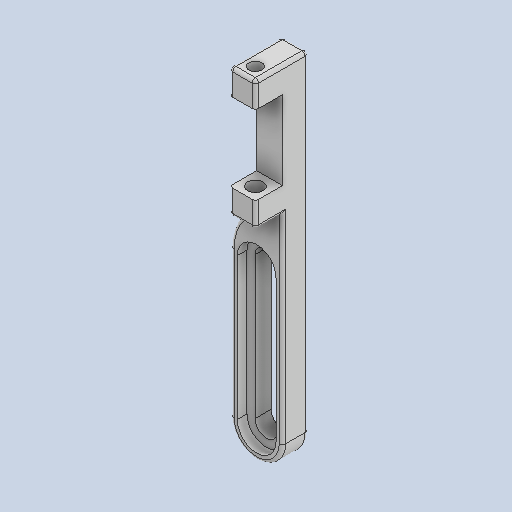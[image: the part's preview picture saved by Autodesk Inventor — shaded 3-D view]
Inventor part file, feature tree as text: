
AUTODESK INVENTOR PART (.ipt)
format: ipt  version: 2025 (Build 290162000, 162)  size: 366,592 bytes
history: native  units: mm
features: sketch x6, extrude x5, fillet x4, reference x4, other x4, plane x1
ambient origin geometry x8: Origin, YZ Plane, XZ Plane, XY Plane, X Axis, Y Axis, Z Axis, Center Point
bodies: Solid1 (feature_tree)
feature tree (24):
  plane  "Work Plane1"
  extrude  "Extrusion1"  Depth=4.0mm
  extrude  "Extrusion2"  Depth=30.0mm
  extrude  "Extrusion3"  Depth=4.0mm
  extrude  "Extrusion4"  Depth=4.0mm TaperAngle=0.0deg
  extrude  "Extrusion5"  Depth=1.5mm TaperAngle=0.0deg
  fillet  "Fillet1"  Radius=3.9mm
  fillet  "Fillet2"  Radius=3.9mm
  fillet  "Fillet3"  Radius=4.2mm
  fillet  "Fillet4"  Radius=2.0mm
  sketch  "Sketch6"  dims[d24=2.0mm d25=4.2mm d26=0.0mm d27=2.4mm d28=10.0mm d29=0.0mm d30=1.0mm d31=2.4mm d32=4.0mm d33=8.0mm d34=0.5mm d35=1.0mm d36=20.0mm]
  sketch  "Sketch1"  dims[d4=21.0mm d6=4.0mm]
  reference  "Reference1"
  reference  "Reference2"
  reference  "Reference3"
  reference  "Reference4"
  sketch  "Sketch2"  dims[d7=135.0deg d8=30.0mm]
  sketch  "Sketch3"  dims[d11=4.0mm d12=22.0mm]
  sketch  "Sketch4"  dims[d13=1.75mm d14=4.0mm d15=0.0mm]
  sketch  "Sketch5"  dims[d16=6.0mm d17=1.5mm d18=0.0mm d19=3.9mm d20=3.9mm d21=4.2mm d22=0.0mm d23=2.0mm]
  other  "<userpath>\Documents\GitHub\miku-voron\Mods\Nozzle Cleaner\nozzlecleaner.iam"
  other  "nozzlecleaner.iam"
  other  "nozzlecleaner:1"
  other  "Assembly1"
